# Revit family: HEATER MIX
name_source: partatom
category: Wyposażenie mechaniczne
revit_build: Autodesk Revit 2018 (Build: 20170927_1515(x64)
units: mm (PartAtom-declared; Revit-internal decimal feet)

## family parameters
Klasyfikacja = Brak
Obiekt nadrzędny = Powierzchnia
Punkt obliczania pomieszczeń = Nie
Tnij formami wycięć po wczytaniu = Nie
Typ części = Normalny
Współdzielony = Nie
Wymiar okrągłego złącza = Użyj średnicy

## types (1)
- HEATER MIX
    Autor = www.archispace.com
    Domyślna rzędna = 1219 mm
    Model = Mix
    Opis = Дестратификатор воздуха MIX
    Producent = Sonninger Sp. z o.o. Sp. k.
    Класс защиты = IP54
    Максимальная высота установки = 15000 mm  [stored 49.2126 ft]
    Максимальный расход воздуха = 5500.0 m³/h
    Масса оборудования = 9.20 kg
    Мощность электродвигателя = 360 W
    Напряжение питания = 230 V
    Уровень шума = 60.5
    Частота вращения двигателя = 1400
    максимальная площадь покрытия = 380 m²
    масса оборудования с водой = 9.20 kg
    материал = Body - PPT material
    минимальная высота установки = 4 mm  [stored 0.0131234 ft]
    минимальный площадь покрытия = 200 m²

note: [stored X ft] marks values corroborated as IEEE doubles in the binary element streams (Revit-internal decimal feet)
